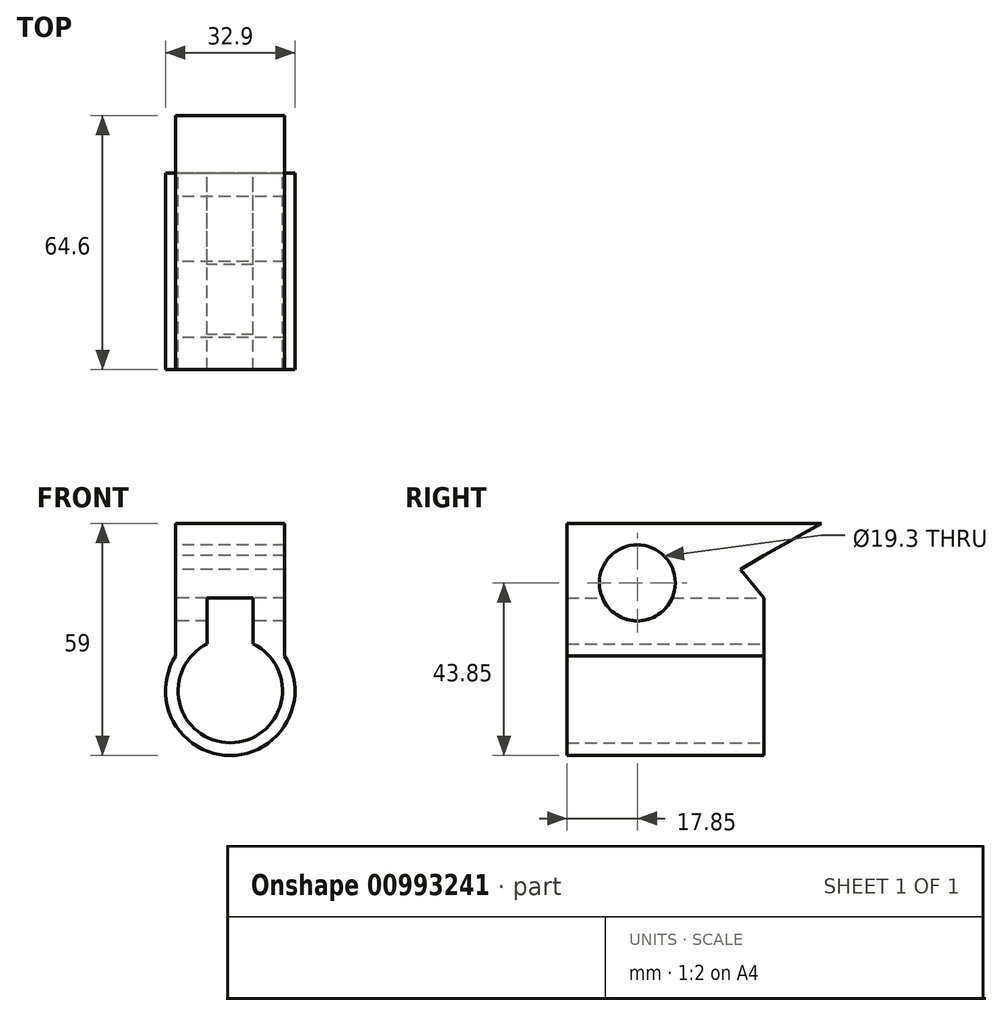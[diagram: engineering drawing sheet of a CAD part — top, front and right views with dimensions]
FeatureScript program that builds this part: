
annotation { "Feature Type Name" : "Feature", "Feature Type Description" : "" }
export const myFeature = defineFeature(function(context is Context, id is Id, definition is map)
    precondition{}
    {
        {
            var Q0;
            Q0=qCreatedBy(makeId("Front.planeOp"),FACE);
            var sketch = newSketch(context, id + "F0", { "sketchPlane" : qUnion([Q0])});
            skArc(sketch, "E0", {"start": v(-13.85, 8.88) * mm, "mid": v(0, -16.45) * mm, "end": v(13.85, 8.88) * mm});
            skCircle(sketch, "E1", {"center": v(0, 0) * mm, "radius": 13.25 * mm});
            skLineSegment(sketch, "E2", {"start": v(-13.85, 42.55) * mm, "end": v(13.85, 42.55) * mm});
            skLineSegment(sketch, "E3", {"start": v(-13.85, 42.55) * mm, "end": v(-13.85, 8.88) * mm});
            skLineSegment(sketch, "E4", {"start": v(13.85, 8.88) * mm, "end": v(13.85, 42.55) * mm});
            skSolve(sketch);
        }
        {
            var Q0;
            Q0 = qSketchRegion(id + "F0", true);
            extrude(context, id + "F1", {"entities" : qUnion([Q0]), "depth" : 50 * mm, "offsetDistance" : 25 * mm});
        }
        {
            var Q0;
            Q0=makeQuery(id+"F1.opExtrude","SWEPT_FACE",FACE,{"disambiguationData":[OSD([sQuery(id+"F0.wireOp",EDGE,"E3")])]});
            var sketch = newSketch(context, id + "F2", { "sketchPlane" : qUnion([Q0])});
            skCircle(sketch, "E5", {"center": v(32.15, 27.4) * mm, "radius": 9.65 * mm});
            skSolve(sketch);
        }
        {
            var Q0;
            Q0 = qSketchRegion(id + "F2", true);
            extrude(context, id + "F3", {"entities" : qUnion([Q0]), "operationType" : NewBodyOperationType.REMOVE, "endBound" : BoundingType.THROUGH_ALL, "oppositeDirection" : true, "depth" : 25 * mm, "offsetDistance" : 25 * mm});
        }
        {
            var Q0;
            Q0=makeQuery(id+"F1.opExtrude","SWEPT_FACE",FACE,{"disambiguationData":[OSD([sQuery(id+"F0.wireOp",EDGE,"E3")])]});
            var sketch = newSketch(context, id + "F4", { "sketchPlane" : qUnion([Q0])});
            skLineSegment(sketch, "E6", {"start": v(6, 30.76) * mm, "end": v(0, 23.55) * mm});
            skLineSegment(sketch, "E7", {"start": v(6, 30.76) * mm, "end": v(0, 34.36) * mm});
            skLineSegment(sketch, "E8", {"start": v(0, 23.55) * mm, "end": v(0, 34.36) * mm});
            skSolve(sketch);
        }
        {
            var Q0;
            Q0 = qSketchRegion(id + "F4", true);
            extrude(context, id + "F5", {"entities" : qUnion([Q0]), "operationType" : NewBodyOperationType.REMOVE, "endBound" : BoundingType.THROUGH_ALL, "oppositeDirection" : true, "depth" : 25 * mm, "offsetDistance" : 25 * mm});
        }
        {
            var Q0;
            Q0=makeQuery(id+"F1.opExtrude","SWEPT_FACE",FACE,{"disambiguationData":[OSD([sQuery(id+"F0.wireOp",EDGE,"E3")])]});
            var sketch = newSketch(context, id + "F6", { "sketchPlane" : qUnion([Q0])});
            skLineSegment(sketch, "E9", {"start": v(0, 34.36) * mm, "end": v(-14.6, 42.55) * mm});
            skLineSegment(sketch, "E10", {"start": v(-14.6, 42.55) * mm, "end": v(0, 42.55) * mm});
            skLineSegment(sketch, "E11", {"start": v(0, 42.55) * mm, "end": v(0, 34.36) * mm});
            skSolve(sketch);
        }
        {
            var Q0;
            Q0 = qSketchRegion(id + "F6", true);
            extrude(context, id + "F7", {"entities" : qUnion([Q0]), "operationType" : NewBodyOperationType.ADD, "oppositeDirection" : true, "depth" : 27.7 * mm, "offsetDistance" : 25 * mm});
        }
        {
            var Q0;
            {var subQ0=sQuery(id+"F0.wireOp",EDGE,"E4");var subQ1=sQuery(id+"F0.wireOp",EDGE,"E1");var subQ2=sQuery(id+"F0.wireOp",EDGE,"E3");var subQ3=sQuery(id+"F0.wireOp",EDGE,"E0");Q0=makeQuery(id+"F5.boolean.opBoolean","SPLIT",FACE,{"disambiguationData":[TD([makeQuery(id+"F1.opExtrude","SWEPT_FACE",FACE,{"disambiguationData":[OSD([subQ3])]})])],"derivedFrom":makeQuery(id+"F1.opExtrude","CAP_FACE",FACE,{"disambiguationData":[OSD([subQ3,subQ1,sQuery(id+"F0.wireOp",EDGE,"E2"),subQ2,subQ0])],"isStart":true})});}
            var sketch = newSketch(context, id + "F8", { "sketchPlane" : qUnion([Q0])});
            skLineSegment(sketch, "E12", {"start": v(5.85, 23.55) * mm, "end": v(5.85, 11.89) * mm});
            skLineSegment(sketch, "E13", {"start": v(5.85, 23.55) * mm, "end": v(-5.85, 23.55) * mm});
            skLineSegment(sketch, "E14", {"start": v(-5.85, 23.55) * mm, "end": v(-5.85, 11.89) * mm});
            skLineSegment(sketch, "E15", {"start": v(5.85, 11.89) * mm, "end": v(-5.85, 11.89) * mm});
            skSolve(sketch);
        }
        {
            var Q0;
            Q0 = qSketchRegion(id + "F8", true);
            var Q1;
            {var subQ0=sQuery(id+"F8.wireOp",EDGE,"E15");Q1=makeQuery(id+"F8.imprint","IMPRINT",FACE,{"disambiguationData":[TD([[makeQuery(id+"F8.imprint","IMPRINT",EDGE,{"derivedFrom":subQ0}),1.0]])]});}
            extrude(context, id + "F9", {"entities" : qUnion([Q0, Q1]), "operationType" : NewBodyOperationType.REMOVE, "endBound" : BoundingType.THROUGH_ALL, "oppositeDirection" : true, "depth" : 25 * mm, "offsetDistance" : 25 * mm});
        }
    });
